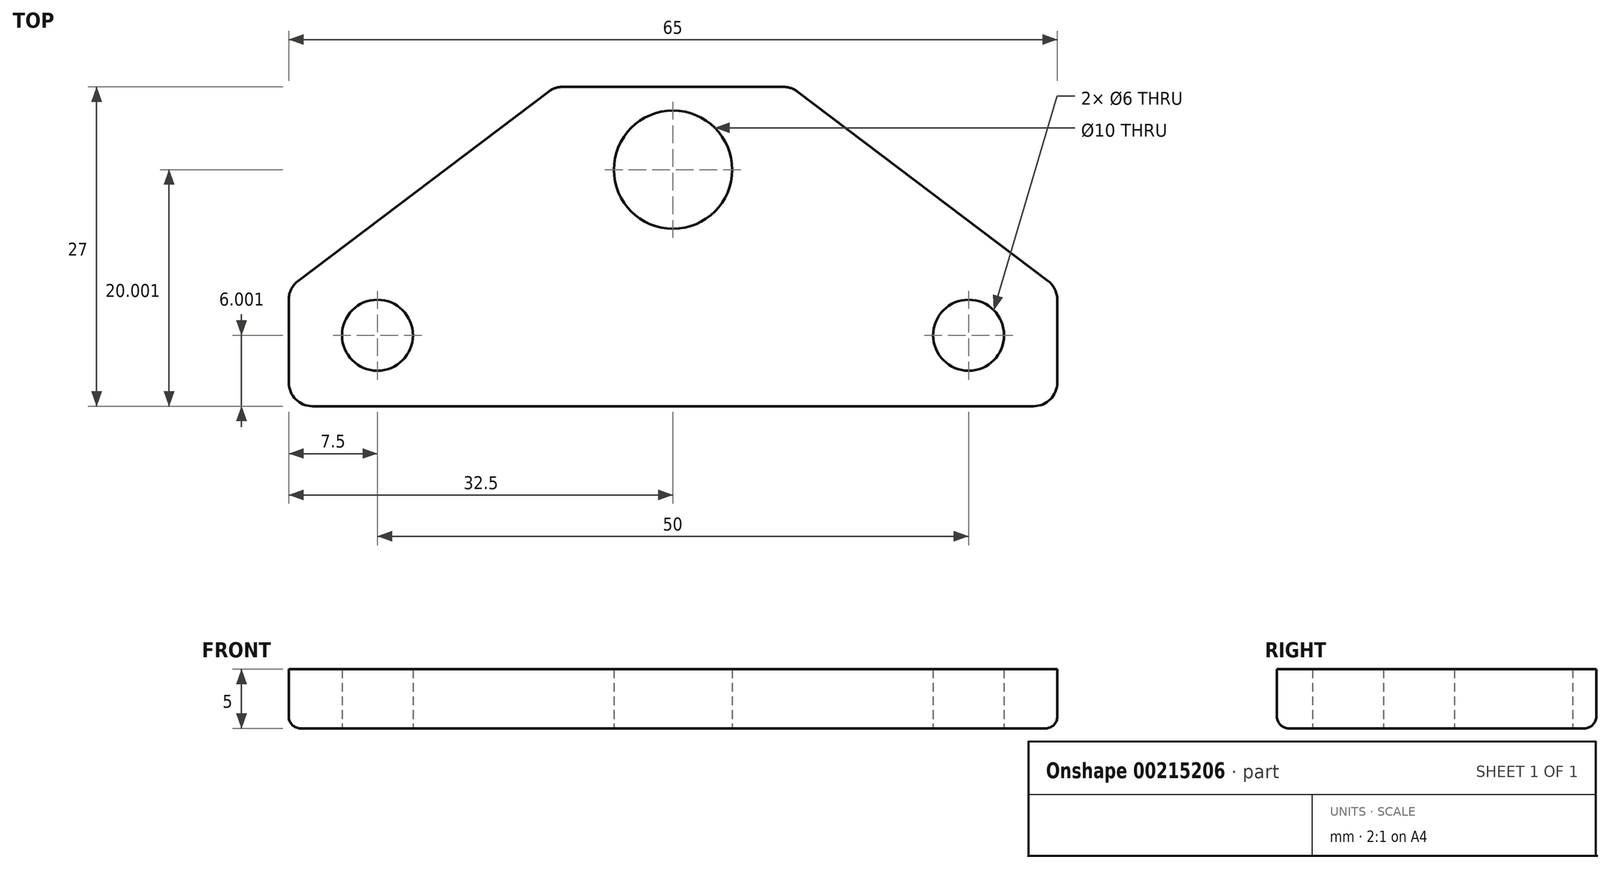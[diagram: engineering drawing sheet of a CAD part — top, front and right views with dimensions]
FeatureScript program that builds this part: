
annotation { "Feature Type Name" : "Feature", "Feature Type Description" : "" }
export const myFeature = defineFeature(function(context is Context, id is Id, definition is map)
    precondition{}
    {
        {
            var Q0;
            Q0=qCreatedBy(makeId("Top.planeOp"),FACE);
            var sketch = newSketch(context, id + "F0", { "sketchPlane" : qUnion([Q0])});
            skLineSegment(sketch, "E0.bottom", {"start": v(-32.5, -34.02) * mm, "end": v(32.5, -34.02) * mm});
            skLineSegment(sketch, "E0.top", {"start": v(-10, -7.02) * mm, "end": v(10, -7.02) * mm});
            skLineSegment(sketch, "E0.left", {"start": v(-32.5, -34.02) * mm, "end": v(-32.5, -24.02) * mm});
            skCircle(sketch, "E1", {"center": v(0, -14.02) * mm, "radius": 5 * mm});
            skLineSegment(sketch, "E2", {"start": v(10, -7.02) * mm, "end": v(32.5, -24.02) * mm});
            skLineSegment(sketch, "E3", {"start": v(-10, -7.02) * mm, "end": v(-32.5, -24.02) * mm});
            skLineSegment(sketch, "E4", {"start": v(32.5, -24.02) * mm, "end": v(32.5, -34.02) * mm});
            skPoint(sketch, "E5.trimOffspring.end.orphan", {"position": v(0, -7.02) * mm});
            skPoint(sketch, "E6.start.orphan", {"position": v(0, -34.02) * mm});
            skCircle(sketch, "E7", {"center": v(-25, -28.02) * mm, "radius": 3 * mm});
            skCircle(sketch, "E8", {"center": v(25, -28.02) * mm, "radius": 3 * mm});
            skSolve(sketch);
        }
        {
            var Q0;
            Q0=makeQuery(id+"F0.imprint","IMPRINT",FACE,{"disambiguationData":[TD([[makeQuery(id+"F0.imprint","IMPRINT",EDGE,{"derivedFrom":sQuery(id+"F0.wireOp",EDGE,"E0.bottom")}),1.0]])]});
            extrude(context, id + "F1", {"entities" : qUnion([Q0]), "depth" : 5 * mm});
        }
        {
            var Q0;
            Q0=makeQuery(id+"F1.opExtrude","SWEPT_EDGE",EDGE,{"disambiguationData":[OSD([sQuery(id+"F0.wireOp",EDGE,"E0.top"),sQuery(id+"F0.wireOp",EDGE,"E3")])]});
            var Q1;
            Q1=makeQuery(id+"F1.opExtrude","SWEPT_EDGE",EDGE,{"disambiguationData":[OSD([sQuery(id+"F0.wireOp",EDGE,"E0.left"),sQuery(id+"F0.wireOp",EDGE,"E3")])]});
            var Q2;
            Q2=makeQuery(id+"F1.opExtrude","SWEPT_EDGE",EDGE,{"disambiguationData":[OSD([sQuery(id+"F0.wireOp",EDGE,"E0.top"),sQuery(id+"F0.wireOp",EDGE,"E2")])]});
            var Q3;
            Q3=makeQuery(id+"F1.opExtrude","SWEPT_EDGE",EDGE,{"disambiguationData":[OSD([sQuery(id+"F0.wireOp",EDGE,"E2"),sQuery(id+"F0.wireOp",EDGE,"E4")])]});
            var Q4;
            Q4=makeQuery(id+"F1.opExtrude","SWEPT_EDGE",EDGE,{"disambiguationData":[OSD([sQuery(id+"F0.wireOp",EDGE,"E0.bottom"),sQuery(id+"F0.wireOp",EDGE,"E0.left")])]});
            var Q5;
            Q5=makeQuery(id+"F1.opExtrude","SWEPT_EDGE",EDGE,{"disambiguationData":[OSD([sQuery(id+"F0.wireOp",EDGE,"E0.bottom"),sQuery(id+"F0.wireOp",EDGE,"E4")])]});
            fillet(context, id + "F2", {"entities" : qUnion([Q0, Q1, Q2, Q3, Q4, Q5]), "radius" : 2 * mm, "tangentPropagation" : true, "allowEdgeOverflow" : false});
        }
        {
            var Q0;
            Q0=makeQuery(id+"F1.opExtrude","CAP_EDGE",EDGE,{"disambiguationData":[OSD([sQuery(id+"F0.wireOp",EDGE,"E3")])],"isStart":true});
            var Q1;
            Q1=makeQuery(id+"F1.opExtrude","CAP_EDGE",EDGE,{"disambiguationData":[OSD([sQuery(id+"F0.wireOp",EDGE,"E0.left")])],"isStart":true});
            var Q2;
            Q2=makeQuery(id+"F1.opExtrude","CAP_EDGE",EDGE,{"disambiguationData":[OSD([sQuery(id+"F0.wireOp",EDGE,"E0.bottom")])],"isStart":true});
            var Q3;
            Q3=makeQuery(id+"F1.opExtrude","CAP_EDGE",EDGE,{"disambiguationData":[OSD([sQuery(id+"F0.wireOp",EDGE,"E4")])],"isStart":true});
            var Q4;
            Q4=makeQuery(id+"F1.opExtrude","CAP_EDGE",EDGE,{"disambiguationData":[OSD([sQuery(id+"F0.wireOp",EDGE,"E2")])],"isStart":true});
            var Q5;
            Q5=makeQuery(id+"F1.opExtrude","CAP_EDGE",EDGE,{"disambiguationData":[OSD([sQuery(id+"F0.wireOp",EDGE,"E0.top")])],"isStart":true});
            fillet(context, id + "F3", {"entities" : qUnion([Q0, Q1, Q2, Q3, Q4, Q5]), "radius" : 1 * mm, "tangentPropagation" : true, "allowEdgeOverflow" : false});
        }
    });
